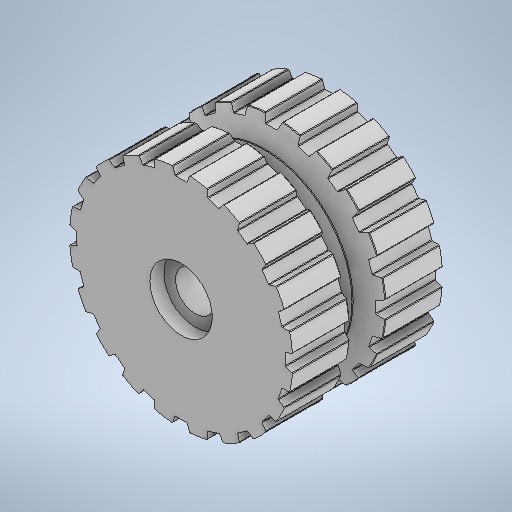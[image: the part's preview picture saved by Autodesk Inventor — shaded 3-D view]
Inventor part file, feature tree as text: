
AUTODESK INVENTOR PART (.ipt)
format: ipt  version: 2025 (Build 290162000, 162)  size: 5,200,896 bytes
history: native  units: mm
features: extrude x4, sketch x4, projected_geometry x3, mirror x2, imported_body x1, plane x1, pattern_circular x1
ambient origin geometry x8: Origin, YZ Plane, XZ Plane, XY Plane, X Axis, Y Axis, Z Axis, Center Point
bodies: Solid1 (feature_tree)
feature tree (16):
  imported_body  "Base1"
  extrude  "Extrusion1"  Depth=10.0mm TaperAngle=0.0deg
  plane  "Work Plane1"
  extrude  "Extrusion2"  Depth=2.0mm
  mirror  "Mirror1"
  extrude  "Extrusion3"  Depth=21.0mm TaperAngle=0.0deg
  mirror  "Mirror2"
  extrude  "Extrusion4"  [1 undecoded]
  pattern_circular  "Circular Pattern1"  [2 undecoded]
  sketch  "Sketch1"  dims[d0=21.0mm d1=0.0mm d2=10.0mm d3=0.0mm]
  projected_geometry  "Projected Loop1"
  sketch  "Sketch2"  dims[d4=0.015mm d5=0.0mm d6=2.0mm]
  sketch  "Sketch3"  dims[d7=5.0mm d8=21.0mm d9=0.0mm]
  projected_geometry  "Projected Loop2"
  sketch  "Sketch4"  dims[d10=80.0mm d11=360.0deg]
  projected_geometry  "Projected Loop3"
note: 3 required parameter values undecoded (feature->parameter linkage not recoverable at this tier; creation-order binding heuristic only, values carry confidence <= 0.55)
